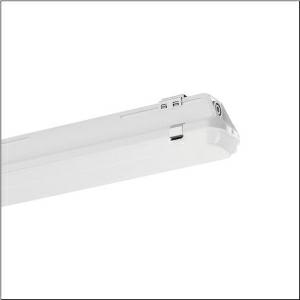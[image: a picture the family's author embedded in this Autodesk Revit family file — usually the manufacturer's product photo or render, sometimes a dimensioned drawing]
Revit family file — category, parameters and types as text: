
# Revit family: monsun_r__21_emergency_51fb207p467c3g_36ef
name_source: partatom
category: Lighting Fixtures
units: mm (PartAtom-declared; Revit-internal decimal feet)

## family parameters
Cut with Voids When Loaded = No
Host = Face
Light Source = No
Part Type = Normal
Room Calculation Point = No
Round Connector Dimension = Use Diameter
Shared = No

## types (1)
- --- (1 x LED, 820 lm, 7.1 W, 4000K)
    Apparent Load = 7 VA
    CIE Flux Codes = 45 75 93 94 100
    Color Rendering = 80
    Color Temperature = 4000K
    Default Elevation = 1800 mm
    Description = Monsun® 21 emergency, damp-proof luminaire, chain hanger, primary optical cover: enclosure, of PC, light emission: direct distribution, primary light characteristic: symmetric, installation type: suspended mounting, surface-mounted, horizontal mounting, vertical mounting, LED, rated luminous flux: 5.460lm, luminous efficacy: 160lm/W, light colour: 840, colour temperature: 4000K, control gear: ON/OFF, with terminal, 4-pole, max. 2.5mm², mains connection: 220..240V, AC, 50/60Hz, rated input power: 38W, control gear: single battery element, battery: LiFePO4, 9Ah, housing, of glass-fibre reinforced polyester, uncoated, bright grey, incl. chain hanger, length: 1.590mm, width: 90mm, height: 88mm, clip for enclosure, of stainless steel (V2A), ceiling mounting element, of stainless steel (V2A), chain hanger, of stainless steel (V2A), protection rating (complete): IP66, insulation class (complete): insulation class I (protective earthing), certification: CE, UKCA, protection symbol: D, impact resistance: IK08, permissible operating ambient temperature: +5..+25°C, standard: EN 50419, EN 60598-2-1, EN 60598-2-22, corresponds to IFS (International Featured Standards) requirements for safety and quality in the food industry, for indoor or canopied outdoor use, no direct snow, no direct sun, no direct rain, LABS conformity tested according to VDMA 24364:2018-05, contact your sales advisor before using the luminaires in applications with unclear chemical exposure, large temperature fluctuations or condensation-forming humidity, packaging unit: 1 piece
    Height = 89 mm
    Lamp = 1 x LED
    Lamp Light Flux = 820 lm
    Lamp Power = 7.1 W
    Lamp count = 1
    Length = 1590 mm
    Luminous efficacy = 115 lm/W
    Manufacturer = Siteco
    ModVariant = No
    Model = 51FB207P467C3G
    Mounting Place = Ceiling
    Mounting Type = Surface mounted
    Number of Poles = 1
    OnlyDefault = Yes
    Power Factor = 1
    Product Name = Monsun® 21 emergency
    Product group = damp-proof luminaire
    ProductGroupID = 301
    Protection Class = Protection class I
    Protection Degree = IP 66
    RLX_Detail_Level = 1
    RLX_Emergency_Light_Flux = 0 lm
    RLX_Emergency_Type = 0
    RLX_Emergency_Type_DB = No
    RlxData = <blob elided: 89049 chars, md5=a5ffff75>
    Socket = socket
    Standby Power = 0 W
    System Light Flux = 820 lm
    System Power = 7 W
    Type Comments = : emergency light operation: 3 h
    Type Image = l_1319656.jpg
    URL = http://relux.com
    VarID = @adj_062711
    Voltage = 0 V
    Weight = 0.00 kg
    Width = 90 mm

## geometry (parser evidence)
native form markers: Blend x4, Sweep x14
no freeform markers — native parametric forms only
